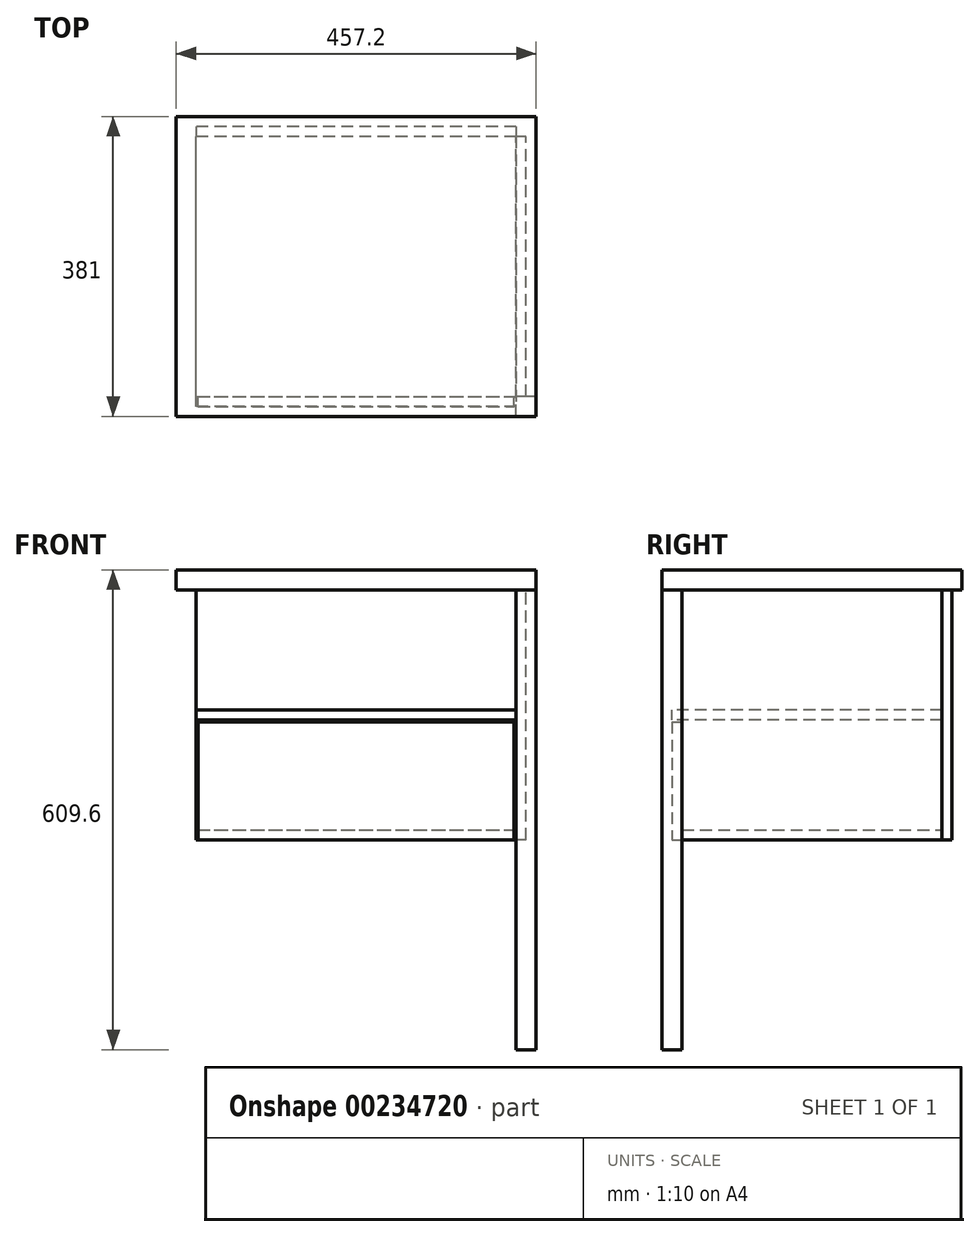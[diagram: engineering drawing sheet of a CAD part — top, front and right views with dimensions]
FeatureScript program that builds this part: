
annotation { "Feature Type Name" : "Feature", "Feature Type Description" : "" }
export const myFeature = defineFeature(function(context is Context, id is Id, definition is map)
    precondition{}
    {
        {
            var Q0;
            Q0=qCreatedBy(makeId("Top.planeOp"),FACE);
            var sketch = newSketch(context, id + "F0", { "sketchPlane" : qUnion([Q0])});
            skLineSegment(sketch, "E0.bottom", {"start": v(228.6, 190.5) * mm, "end": v(-228.6, 190.5) * mm});
            skLineSegment(sketch, "E0.top", {"start": v(228.6, -190.5) * mm, "end": v(-228.6, -190.5) * mm});
            skLineSegment(sketch, "E0.left", {"start": v(228.6, 190.5) * mm, "end": v(228.6, -190.5) * mm});
            skLineSegment(sketch, "E0.right", {"start": v(-228.6, 190.5) * mm, "end": v(-228.6, -190.5) * mm});
            skPoint(sketch, "E0.middle", {"position": v(0, 0) * mm});
            skSolve(sketch);
        }
        {
            var Q0;
            Q0 = qSketchRegion(id + "F0", true);
            extrude(context, id + "F1", {"entities" : qUnion([Q0]), "depth" : 25.4 * mm});
        }
        {
            var Q0;
            Q0=makeQuery(id+"F1.opExtrude","CAP_FACE",FACE,{"disambiguationData":[OSD([sQuery(id+"F0.wireOp",EDGE,"E0.bottom"),sQuery(id+"F0.wireOp",EDGE,"E0.top"),sQuery(id+"F0.wireOp",EDGE,"E0.left"),sQuery(id+"F0.wireOp",EDGE,"E0.right")])],"isStart":true});
            var sketch = newSketch(context, id + "F2", { "sketchPlane" : qUnion([Q0])});
            skLineSegment(sketch, "E1.bottom", {"start": v(228.6, 190.5) * mm, "end": v(203.2, 190.5) * mm});
            skLineSegment(sketch, "E1.top", {"start": v(228.6, 165.1) * mm, "end": v(203.2, 165.1) * mm});
            skLineSegment(sketch, "E1.left", {"start": v(228.6, 190.5) * mm, "end": v(228.6, 165.1) * mm});
            skLineSegment(sketch, "E1.right", {"start": v(203.2, 190.5) * mm, "end": v(203.2, 165.1) * mm});
            skSolve(sketch);
        }
        {
            var Q0;
            Q0 = qSketchRegion(id + "F2", true);
            extrude(context, id + "F3", {"entities" : qUnion([Q0]), "depth" : 584.2 * mm});
        }
        {
            var Q0;
            Q0=qCreatedBy(makeId("Top.planeOp"),FACE);
            cPlane(context, id + "F4", {"entities" : qUnion([Q0]), "cplaneType" : CPlaneType.OFFSET, "offset" : 304.8 * mm, "oppositeDirection" : true, "width" : 152.4 * mm, "height" : 152.4 * mm});
        }
        {
            var Q0;
            Q0=qCreatedBy(id+"F4.planeOp",FACE);
            var sketch = newSketch(context, id + "F5", { "sketchPlane" : qUnion([Q0])});
            skLineSegment(sketch, "E2.bottom", {"start": v(-203.2, -165.1) * mm, "end": v(203.2, -165.1) * mm});
            skLineSegment(sketch, "E2.top", {"start": v(-203.2, 165.1) * mm, "end": v(203.2, 165.1) * mm});
            skLineSegment(sketch, "E2.left", {"start": v(-203.2, -165.1) * mm, "end": v(-203.2, 165.1) * mm});
            skLineSegment(sketch, "E2.right", {"start": v(203.2, -165.1) * mm, "end": v(203.2, 165.1) * mm});
            skPoint(sketch, "E2.middle", {"position": v(0, 0) * mm});
            skSolve(sketch);
        }
        {
            var Q0;
            Q0=makeQuery(id+"F5.imprint","IMPRINT",FACE,{"disambiguationData":[TD([[makeQuery(id+"F5.imprint","IMPRINT",EDGE,{"derivedFrom":sQuery(id+"F5.wireOp",EDGE,"E2.bottom")}),1.0]])]});
            extrude(context, id + "F6", {"entities" : qUnion([Q0]), "oppositeDirection" : true, "depth" : 12.7 * mm});
        }
        {
            var Q0;
            Q0=qCreatedBy(makeId("Right.planeOp"),FACE);
            cPlane(context, id + "F7", {"entities" : qUnion([Q0]), "cplaneType" : CPlaneType.OFFSET, "offset" : 203.2 * mm, "width" : 152.4 * mm, "height" : 152.4 * mm});
        }
        {
            var Q0;
            Q0=qCreatedBy(id+"F7.planeOp",FACE);
            var sketch = newSketch(context, id + "F8", { "sketchPlane" : qUnion([Q0])});
            skLineSegment(sketch, "E3.bottom", {"start": v(-165.1, -317.5) * mm, "end": v(165.1, -317.5) * mm});
            skLineSegment(sketch, "E3.top", {"start": v(-165.1, 0) * mm, "end": v(165.1, 0) * mm});
            skLineSegment(sketch, "E3.left", {"start": v(-165.1, -317.5) * mm, "end": v(-165.1, 0) * mm});
            skLineSegment(sketch, "E3.right", {"start": v(165.1, -317.5) * mm, "end": v(165.1, 0) * mm});
            skSolve(sketch);
        }
        {
            var Q0;
            Q0 = qSketchRegion(id + "F8", true);
            extrude(context, id + "F9", {"entities" : qUnion([Q0]), "depth" : 12.7 * mm});
        }
        {
            var Q0;
            Q0=qCreatedBy(makeId("Front.planeOp"),FACE);
            cPlane(context, id + "F10", {"entities" : qUnion([Q0]), "cplaneType" : CPlaneType.OFFSET, "offset" : 165.1 * mm, "oppositeDirection" : true, "width" : 152.4 * mm, "height" : 152.4 * mm});
        }
        {
            var Q0;
            Q0=qCreatedBy(id+"F10.planeOp",FACE);
            var sketch = newSketch(context, id + "F11", { "sketchPlane" : qUnion([Q0])});
            skLineSegment(sketch, "E4.bottom", {"start": v(203.2, -317.5) * mm, "end": v(-203.2, -317.5) * mm});
            skLineSegment(sketch, "E4.top", {"start": v(203.2, 0) * mm, "end": v(-203.2, 0) * mm});
            skLineSegment(sketch, "E4.left", {"start": v(203.2, -317.5) * mm, "end": v(203.2, 0) * mm});
            skLineSegment(sketch, "E4.right", {"start": v(-203.2, -317.5) * mm, "end": v(-203.2, 0) * mm});
            skSolve(sketch);
        }
        {
            var Q0;
            Q0=makeQuery(id+"F11.imprint","IMPRINT",FACE,{"disambiguationData":[TD([[makeQuery(id+"F11.imprint","IMPRINT",EDGE,{"derivedFrom":sQuery(id+"F11.wireOp",EDGE,"E4.bottom")}),-1.0]])]});
            extrude(context, id + "F12", {"entities" : qUnion([Q0]), "oppositeDirection" : true, "depth" : 12.7 * mm});
        }
        {
            var Q0;
            Q0=qCreatedBy(makeId("Front.planeOp"),FACE);
            cPlane(context, id + "F13", {"entities" : qUnion([Q0]), "cplaneType" : CPlaneType.OFFSET, "offset" : 165.1 * mm, "width" : 152.4 * mm, "height" : 152.4 * mm});
        }
        {
            var Q0;
            Q0=qCreatedBy(id+"F13.planeOp",FACE);
            var sketch = newSketch(context, id + "F14", { "sketchPlane" : qUnion([Q0])});
            skLineSegment(sketch, "E5.bottom", {"start": v(-200.66, -167.64) * mm, "end": v(200.66, -167.64) * mm});
            skLineSegment(sketch, "E5.top", {"start": v(-200.66, -317.5) * mm, "end": v(200.66, -317.5) * mm});
            skLineSegment(sketch, "E5.left", {"start": v(-200.66, -167.64) * mm, "end": v(-200.66, -317.5) * mm});
            skLineSegment(sketch, "E5.right", {"start": v(200.66, -167.64) * mm, "end": v(200.66, -317.5) * mm});
            skPoint(sketch, "E5.middle", {"position": v(0, -242.57) * mm});
            skSolve(sketch);
        }
        {
            var Q0;
            Q0=makeQuery(id+"F14.imprint","IMPRINT",FACE,{"disambiguationData":[TD([[makeQuery(id+"F14.imprint","IMPRINT",EDGE,{"derivedFrom":sQuery(id+"F14.wireOp",EDGE,"E5.bottom")}),-1.0]])]});
            extrude(context, id + "F15", {"entities" : qUnion([Q0]), "depth" : 12.7 * mm});
        }
        {
            var Q0;
            Q0=qCreatedBy(makeId("Top.planeOp"),FACE);
            cPlane(context, id + "F16", {"entities" : qUnion([Q0]), "cplaneType" : CPlaneType.OFFSET, "offset" : 152.4 * mm, "oppositeDirection" : true, "width" : 152.4 * mm, "height" : 152.4 * mm});
        }
        {
            var Q0;
            Q0=qCreatedBy(id+"F16.planeOp",FACE);
            var sketch = newSketch(context, id + "F17", { "sketchPlane" : qUnion([Q0])});
            skLineSegment(sketch, "E6.0", {"start": v(203.2, 165.1) * mm, "end": v(-203.2, 165.1) * mm});
            skLineSegment(sketch, "E7", {"start": v(203.2, 165.1) * mm, "end": v(203.2, -177.8) * mm});
            skLineSegment(sketch, "E8", {"start": v(203.2, -177.8) * mm, "end": v(-203.2, -177.8) * mm});
            skLineSegment(sketch, "E9", {"start": v(-203.2, -177.8) * mm, "end": v(-203.2, 165.1) * mm});
            skPoint(sketch, "E10", {"position": v(0, 0) * mm});
            skSolve(sketch);
        }
        {
            var Q0;
            Q0=makeQuery(id+"F17.imprint","IMPRINT",FACE,{"disambiguationData":[TD([[makeQuery(id+"F17.imprint","IMPRINT",EDGE,{"derivedFrom":sQuery(id+"F17.wireOp",EDGE,"E6.0")}),1.0]])]});
            extrude(context, id + "F18", {"entities" : qUnion([Q0]), "oppositeDirection" : true, "depth" : 12.7 * mm});
        }
    });
